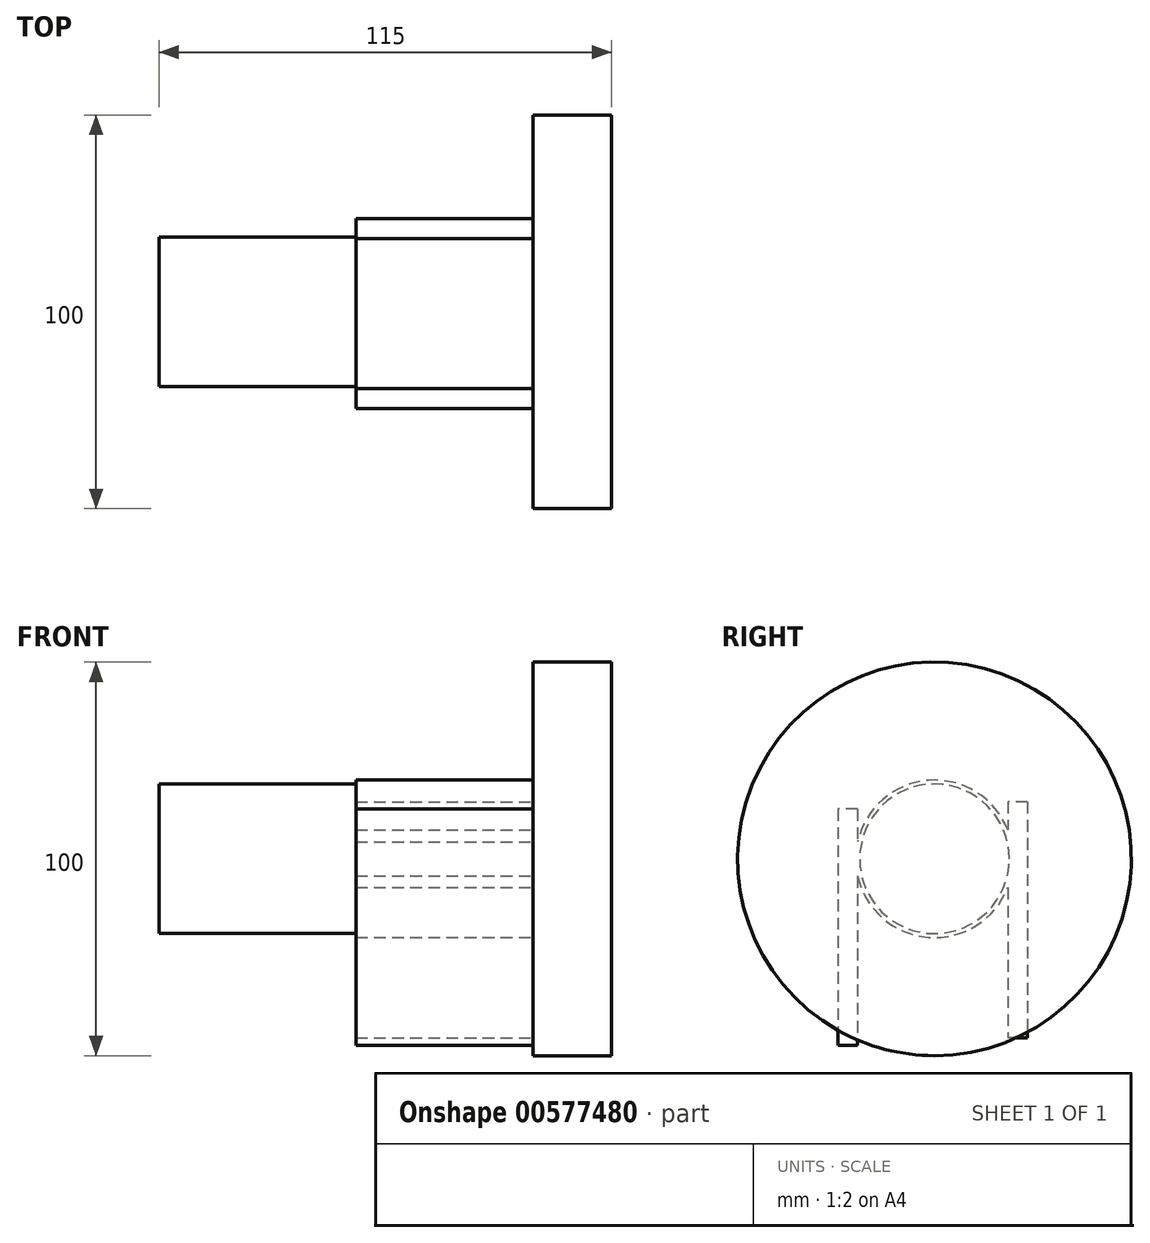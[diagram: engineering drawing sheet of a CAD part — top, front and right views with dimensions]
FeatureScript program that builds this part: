
annotation { "Feature Type Name" : "Feature", "Feature Type Description" : "" }
export const myFeature = defineFeature(function(context is Context, id is Id, definition is map)
    precondition{}
    {
        {
            var Q0;
            Q0=qCreatedBy(makeId("Right.planeOp"),FACE);
            var sketch = newSketch(context, id + "F0", { "sketchPlane" : qUnion([Q0])});
            skCircle(sketch, "E0", {"center": v(0, 57.61) * mm, "radius": 50 * mm});
            skSolve(sketch);
        }
        {
            var Q0;
            Q0=makeQuery(id+"F0.imprint","IMPRINT",FACE,{"disambiguationData":[TD([[makeQuery(id+"F0.imprint","IMPRINT",EDGE,{"derivedFrom":sQuery(id+"F0.wireOp",EDGE,"E0")}),1.0]])]});
            extrude(context, id + "F1", {"entities" : qUnion([Q0]), "depth" : 20 * mm});
        }
        {
            var Q0;
            Q0=makeQuery(id+"F1.opExtrude","CAP_FACE",FACE,{"disambiguationData":[OSD([sQuery(id+"F0.wireOp",EDGE,"E0")])],"isStart":true});
            var sketch = newSketch(context, id + "F2", { "sketchPlane" : qUnion([Q0])});
            skCircle(sketch, "E1", {"center": v(0, 57.61) * mm, "radius": 20 * mm});
            skSolve(sketch);
        }
        {
            var Q0;
            Q0=qSketchRegion(id+"F2",true);
            extrude(context, id + "F3", {"entities" : qUnion([Q0]), "operationType" : NewBodyOperationType.ADD, "depth" : 45 * mm});
        }
        {
            var Q0;
            Q0=qCreatedBy(makeId("Right.planeOp"),FACE);
            var sketch = newSketch(context, id + "F4", { "sketchPlane" : qUnion([Q0])});
            skLineSegment(sketch, "E2.bottom", {"start": v(-19.52, 70.25) * mm, "end": v(-24.52, 70.25) * mm});
            skLineSegment(sketch, "E2.top", {"start": v(-19.52, 10.25) * mm, "end": v(-24.52, 10.25) * mm});
            skLineSegment(sketch, "E2.left", {"start": v(-19.52, 70.25) * mm, "end": v(-19.52, 10.25) * mm});
            skLineSegment(sketch, "E2.right", {"start": v(-24.52, 70.25) * mm, "end": v(-24.52, 10.25) * mm});
            skPoint(sketch, "E2.middle", {"position": v(-22.02, 40.25) * mm});
            skSolve(sketch);
        }
        {
            var Q0;
            Q0=qSketchRegion(id+"F4",true);
            extrude(context, id + "F5", {"entities" : qUnion([Q0]), "operationType" : NewBodyOperationType.ADD, "oppositeDirection" : true, "depth" : 45 * mm, "offsetDistance" : 25 * mm});
        }
        {
            var Q0;
            Q0=makeQuery(id+"F5.boolean.opBoolean","MERGE",FACE,{"derivedFrom":[makeQuery(id+"F3.opExtrude","CAP_FACE",FACE,{"disambiguationData":[OSD([sQuery(id+"F2.wireOp",EDGE,"E1")])],"isStart":false}),makeQuery(id+"F5.opExtrude","CAP_FACE",FACE,{"disambiguationData":[OSD([sQuery(id+"F4.wireOp",EDGE,"E2.bottom"),sQuery(id+"F4.wireOp",EDGE,"E2.top"),sQuery(id+"F4.wireOp",EDGE,"E2.left"),sQuery(id+"F4.wireOp",EDGE,"E2.right")])],"isStart":false})]});
            var sketch = newSketch(context, id + "F6", { "sketchPlane" : qUnion([Q0])});
            skCircle(sketch, "E3", {"center": v(0, 57.61) * mm, "radius": 19 * mm});
            skSolve(sketch);
        }
        {
            var Q0;
            Q0=qSketchRegion(id+"F6",true);
            extrude(context, id + "F7", {"entities" : qUnion([Q0]), "operationType" : NewBodyOperationType.ADD, "depth" : 50 * mm});
        }
        {
            var Q0;
            Q0=qCreatedBy(makeId("Right.planeOp"),FACE);
            var sketch = newSketch(context, id + "F8", { "sketchPlane" : qUnion([Q0])});
            skLineSegment(sketch, "E4.bottom", {"start": v(23.62, 72.11) * mm, "end": v(18.62, 72.11) * mm});
            skLineSegment(sketch, "E4.top", {"start": v(23.62, 12.11) * mm, "end": v(18.62, 12.11) * mm});
            skLineSegment(sketch, "E4.left", {"start": v(23.62, 72.11) * mm, "end": v(23.62, 12.11) * mm});
            skLineSegment(sketch, "E4.right", {"start": v(18.62, 72.11) * mm, "end": v(18.62, 12.11) * mm});
            skPoint(sketch, "E4.middle", {"position": v(21.12, 42.11) * mm});
            skSolve(sketch);
        }
        {
            var Q0;
            Q0=qSketchRegion(id+"F8",true);
            extrude(context, id + "F9", {"entities" : qUnion([Q0]), "operationType" : NewBodyOperationType.ADD, "oppositeDirection" : true, "depth" : 45 * mm});
        }
    });
